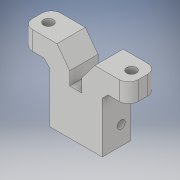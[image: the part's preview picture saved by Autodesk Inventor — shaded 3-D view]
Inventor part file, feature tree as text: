
AUTODESK INVENTOR PART (.ipt)
format: ipt  version: 2018 (Build 220112000, 112)  size: 212,480 bytes
history: native  units: in
note: dims shown in document units (in); Inventor stores cm internally (conversion verified against a paired STEP export)
features: extrude x8, sketch x8, mirror x1, fillet x1, chamfer x1, projected_geometry x1
ambient origin geometry x8: Origin, YZ Plane, XZ Plane, XY Plane, X Axis, Y Axis, Z Axis, Center Point
bodies: Solid1 (feature_tree)
feature tree (20):
  extrude  "Extrusion1"  Depth=1.1811in
  extrude  "Extrusion2"  Depth=0.1575in
  extrude  "Extrusion3"  Depth=0.3937in
  mirror  "Mirror1"
  extrude  "Extrusion4"  Depth=0.2362in
  fillet  "Fillet1"  Radius=0.2362in
  chamfer  "Chamfer1"  Distance=0.3937in
  extrude  "Extrusion7"  Depth=0.1969in TaperAngle=0.0deg
  extrude  "Extrusion8"  Depth=0.3228in
  extrude  "Extrusion5"  Depth=0.3937in
  extrude  "Extrusion9"  Depth=0.1969in TaperAngle=0.0deg
  sketch  "Sketch1"  dims[d0=0.7874in d1=1.1811in]
  sketch  "Sketch2"  dims[d2=0.1575in d3=0.1575in]
  sketch  "Sketch3"  dims[d4=0.5512in d5=0.3937in]
  sketch  "Sketch4"  dims[d6=0.5906in d7=0.0in d8=0.2047in d9=0.2362in]
  sketch  "Sketch6"  dims[d10=0.2362in d11=0.3937in d12=0.0in]
  sketch  "Sketch8"  dims[d13=0.3228in d17=0.1969in d18=0.0in]
  sketch  "Sketch9"  dims[d22=0.3504in d23=0.3228in]
  sketch  "Sketch11"  dims[d24=0.1654in d25=0.3937in d27=0.1969in d28=0.0in d29=0.2559in d30=0.7874in d32=0.1969in d33=0.0in d37=0.1969in d38=0.1181in d39=0.0787in d40=45.0deg d41=0.1181in d42=0.0in d44=0.7874in d45=0.1181in d46=0.0in d47=0.3543in d48=0.1575in d49=0.1654in d50=0.1181in d51=0.0in]
  projected_geometry  "Projected Loop1"
